SOLIDWORKS PART (.sldprt)
format: sldprt  version: not decoded by parser v0  size: 155,136 bytes
history: native  units: mm
features: sketch x3, cut_revolve x2, material x1, extrude x1, pattern_linear x1, chamfer x1 (+12 scaffold rows collapsed)
feature tree (21):
  scaffold x12  (default folders/planes/origin — collapsed)
  material  "Material <not specified>"
  sketch  "Sketch1"  dims[Hex Flats=4.7625mm]
  extrude  "Extrude1"  Depth=1.5875mm Height=1.5875mm
  sketch  "Sketch3"  dims[c1.D1=~0.569483mm c2.D1=45.0deg c2.D2=4.7625mm]
  cut_revolve  "Cut-Revolve2"  Angle=360deg
  sketch  "Sketch2"  dims[c1.D1=1.524mm c1.D2=~0.039688mm c1.D3=~0.079375mm c1.D4=0.3175mm c1.D5=~0.099129mm c2.D5=60.0deg c2.D1=~0.142294mm c3.D1=60.0deg c3.Pitch=~0.453571mm c3.Major Dia.=2.1844mm c3.D4=~0.079375mm c3.D5=~0.056696mm c3.D2=~0.113393mm]
  cut_revolve  "Cut-Revolve1"  Angle=360deg
  pattern_linear  "LPattern2"  Count1=4 Count2=1 Spacing1=0.453571mm Spacing2=50mm
  chamfer  "Chamfer1"  Distance=0.226786mm Angle=45deg
decode coverage: 8 of 8 modeling features carry decoded parameters
note: ~ marks probable driven/reference dimensions
note: suppression state not decoded; provenance and decode notes live in map.json
